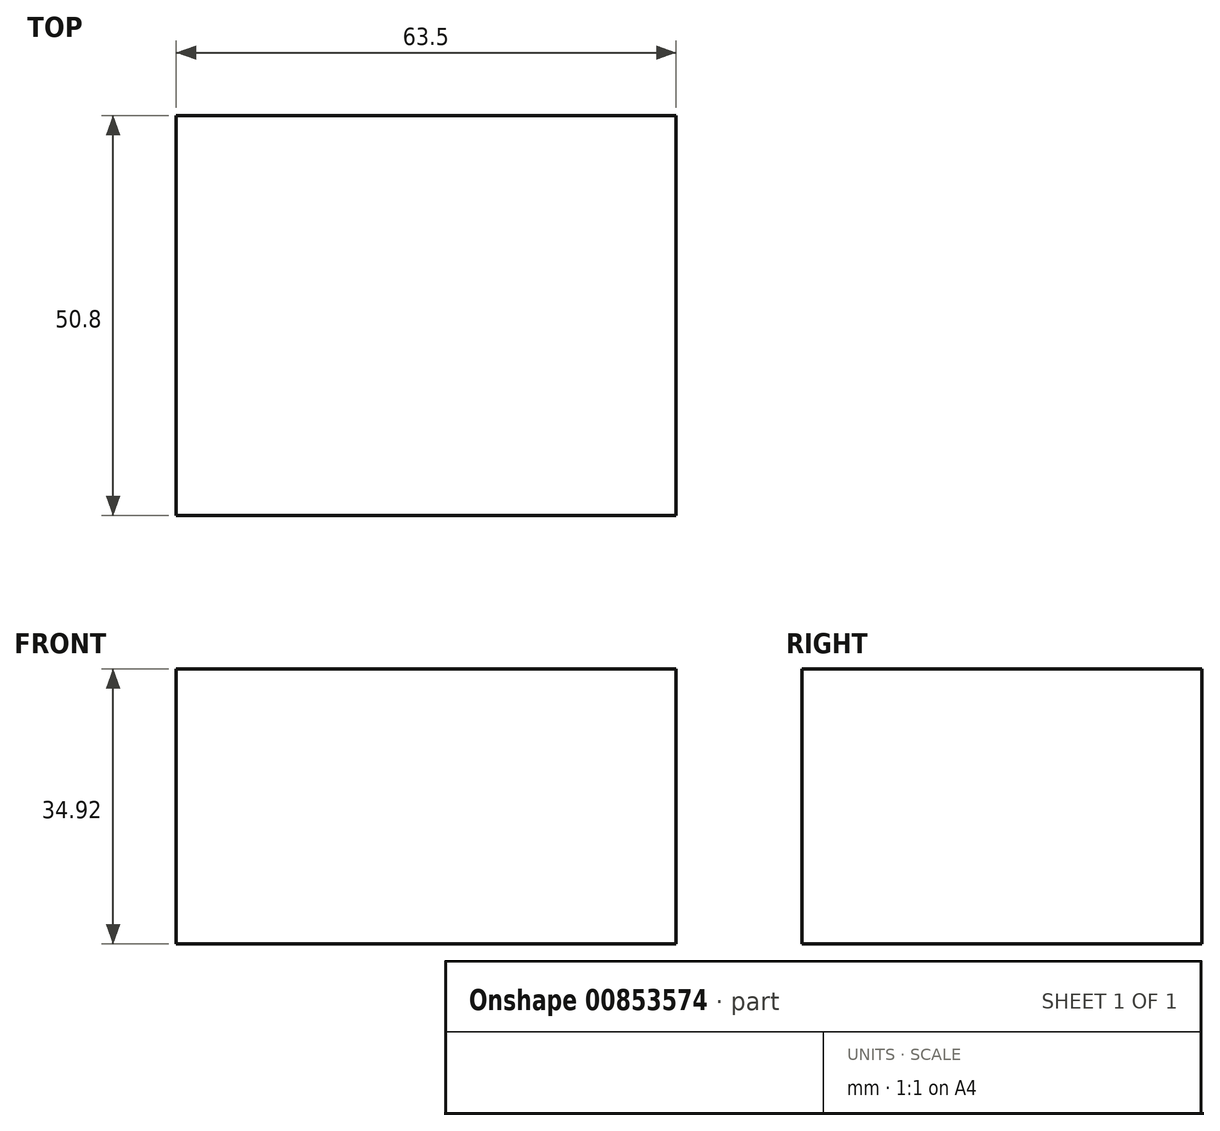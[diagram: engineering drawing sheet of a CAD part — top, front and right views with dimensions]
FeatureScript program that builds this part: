
annotation { "Feature Type Name" : "Feature", "Feature Type Description" : "" }
export const myFeature = defineFeature(function(context is Context, id is Id, definition is map)
    precondition{}
    {
        {
            var Q0;
            Q0=qCreatedBy(makeId("Front.planeOp"),FACE);
            var sketch = newSketch(context, id + "F0", { "sketchPlane" : qUnion([Q0])});
            skLineSegment(sketch, "E0", {"start": v(-35.48, 34.92) * mm, "end": v(28.02, 34.92) * mm});
            skLineSegment(sketch, "E1", {"start": v(28.02, 34.92) * mm, "end": v(28.02, 0) * mm});
            skLineSegment(sketch, "E2", {"start": v(-35.48, 34.92) * mm, "end": v(-35.48, 0) * mm});
            skLineSegment(sketch, "E3", {"start": v(-35.48, 0) * mm, "end": v(28.02, 0) * mm});
            skSolve(sketch);
        }
        {
            var Q0;
            Q0 = qSketchRegion(id + "F0", true);
            var Q1;
            Q1=sQuery(id+"F0.wireOp",EDGE,"E3");
            var Q2;
            Q2=sQuery(id+"F0.wireOp",EDGE,"E2");
            var Q3;
            Q3=sQuery(id+"F0.wireOp",EDGE,"E1");
            var Q4;
            Q4=sQuery(id+"F0.wireOp",EDGE,"E0");
            extrude(context, id + "F1", {"entities" : qUnion([Q0]), "surfaceOperationType" : NewSurfaceOperationType.ADD, "surfaceEntities" : qUnion([Q1, Q2, Q3, Q4]), "oppositeDirection" : true, "depth" : 50.8 * mm, "offsetDistance" : 25.4 * mm});
        }
    });
